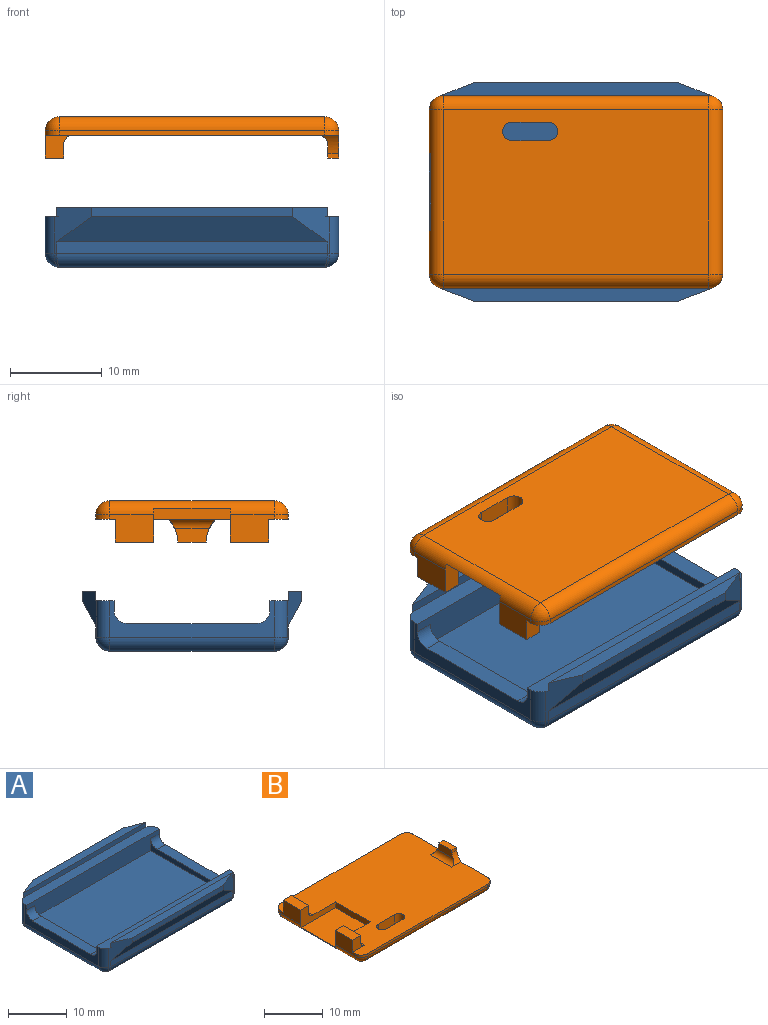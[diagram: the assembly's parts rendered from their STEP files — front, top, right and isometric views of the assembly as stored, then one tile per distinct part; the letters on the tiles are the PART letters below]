
ASSEMBLY  parts=2 mates=1
PART A: 46 faces, bbox 32x24x6.5 mm
  f0: plane 32x2mm, normal (0,0,1), area 63mm2, adj f1,f3,f10,f14,f22,f25,f36,f40
  f1: plane 17.97x4mm, normal (1,0,0), area 30.3mm2, adj f0,f5,f8,f10,f13,f27,f34,f40
  f2: plane 29.5x1.25mm, normal (0,1,0), area 36.9mm2, adj f19,f23,f24,f28
  f3: plane 17.97x4mm, normal (-1,0,0), area 30.3mm2, adj f0,f5,f8,f10,f12,f32,f36,f38
  f4: plane 29.5x1.25mm, normal (0,-1,0), area 36.9mm2, adj f16,f22,f25,f31
  f5: plane 32x2mm, normal (0,0,1), area 63mm2, adj f1,f3,f8,f18,f23,f24,f34,f38
  f6: plane 29x18mm, normal (0,0,-1), area 522mm2, adj f26,f27,f28,f29,f30,f31,f32,f33
  f7: plane 17x2.5mm, normal (-1,0,0), area 18mm2, adj f8,f10,f11,f13,f44,f45
  f8: plane 32x3.5mm, normal (0,-1,0), area 102mm2, adj f1,f3,f5,f7,f9,f11,f43,f44
  f9: plane 17x2.5mm, normal (1,0,0), area 18mm2, adj f8,f10,f11,f12,f42,f43
  f10: plane 32x3.5mm, normal (0,1,0), area 102mm2, adj f0,f1,f3,f7,f9,f11,f42,f45
  f11: plane 28x17mm, normal (0,0,1), area 476mm2, adj f7,f8,f9,f10
  f12: plane 14x2mm, normal (0,0,1), area 28mm2, adj f3,f9,f42,f43
  f13: plane 14x2mm, normal (0,0,1), area 28mm2, adj f1,f7,f44,f45
  f14: plane 29.5x1mm, normal (0,1,0), area 29.5mm2, adj f0,f17,f22,f25
  f15: plane 22x1mm, normal (0,-1,0), area 22mm2, adj f16,f17,f22,f25
  f16: plane 29.5x2.75mm, normal (0,-0.88,-0.48), area 80.7mm2, adj f4,f15,f22,f25
  f17: plane 29.5x1.5mm, normal (0,0,1), area 38.6mm2, adj f14,f15,f22,f25
  f18: plane 29.5x1mm, normal (0,-1,0), area 29.5mm2, adj f5,f21,f23,f24
  f19: plane 29.5x2.75mm, normal (0,0.88,-0.48), area 80.7mm2, adj f2,f20,f23,f24
  f20: plane 22x1mm, normal (0,1,0), area 22mm2, adj f19,f21,f23,f24
  f21: plane 29.5x1.5mm, normal (0,0,1), area 38.6mm2, adj f18,f20,f23,f24
  f22: plane 5x4.06mm, normal (0.37,-0.93,0), area 10.9mm2, adj f0,f4,f14,f15,f16,f17,f29,f40
  f23: plane 5x4.06mm, normal (-0.37,0.93,0), area 10.9mm2, adj f2,f5,f18,f19,f20,f21,f30,f38
  f24: plane 5x4.06mm, normal (0.37,0.93,0), area 10.9mm2, adj f2,f5,f18,f19,f20,f21,f26,f34
  f25: plane 5x4.06mm, normal (-0.37,-0.93,0), area 10.9mm2, adj f0,f4,f14,f15,f16,f17,f33,f36
  f26: cylinder r=1.5mm len=1.52mm, axis (0.93,-0.37,0), area 0.5mm2, adj f6,f24,f28,f35
  f27: cylinder r=1.5mm len=17.97mm, axis (0,1,0), area 42.3mm2, adj f1,f6,f35,f41
  f28: cylinder r=1.5mm len=29.5mm, axis (-1,0,0), area 69mm2, adj f2,f6,f26,f30
  f29: cylinder r=1.5mm len=1.52mm, axis (-0.93,-0.37,0), area 0.5mm2, adj f6,f22,f31,f41
  f30: cylinder r=1.5mm len=1.52mm, axis (-0.93,-0.37,0), area 0.5mm2, adj f6,f23,f28,f39
  f31: cylinder r=1.5mm len=29.5mm, axis (1,0,0), area 69mm2, adj f4,f6,f29,f33
  f32: cylinder r=1.5mm len=17.97mm, axis (0,-1,0), area 42.3mm2, adj f3,f6,f37,f39
  f33: cylinder r=1.5mm len=1.52mm, axis (0.93,-0.37,0), area 0.5mm2, adj f6,f25,f31,f37
  f34: cylinder r=1.5mm len=4mm, axis (0,0,1), area 7.1mm2, adj f1,f5,f24,f35
  f35: sphere r=1.5mm, area 2.7mm2, adj f26,f27,f34
  f36: cylinder r=1.5mm len=4mm, axis (0,0,1), area 7.1mm2, adj f0,f3,f25,f37
  f37: sphere r=1.5mm, area 2.7mm2, adj f32,f33,f36
  f38: cylinder r=1.5mm len=4mm, axis (0,0,-1), area 7.1mm2, adj f3,f5,f23,f39
  f39: sphere r=1.5mm, area 2.7mm2, adj f30,f32,f38
  f40: cylinder r=1.5mm len=4mm, axis (0,0,-1), area 7.1mm2, adj f0,f1,f22,f41
  f41: sphere r=1.5mm, area 2.7mm2, adj f27,f29,f40
  f42: cylinder r=1.5mm len=2mm, axis (1,0,0), area 4.7mm2, adj f3,f9,f10,f12
  f43: cylinder r=1.5mm len=2mm, axis (-1,0,0), area 4.7mm2, adj f3,f8,f9,f12
  f44: cylinder r=1.5mm len=2mm, axis (-1,0,0), area 4.7mm2, adj f1,f7,f8,f13
  f45: cylinder r=1.5mm len=2mm, axis (1,0,0), area 4.7mm2, adj f1,f7,f10,f13
PART B: 42 faces, bbox 32x21x4.5 mm
  f0: plane 4.8x3mm, normal (-1,0,0), area 12.9mm2, adj f1,f2,f9,f22,f24,f30
  f1: plane 32x21mm, normal (0,0,1), area 551mm2, adj f0,f3,f5,f6,f7,f9,f11,f13
  f2: cylinder r=1.5mm len=18mm, axis (0,-1,0), area 36.3mm2, adj f0,f7,f8,f10,f15,f22,f26,f29
  f3: plane 18x3mm, normal (1,0,0), area 18.4mm2, adj f1,f11,f16,f19,f20,f21,f32,f33
  f4: plane 3.79x1.5mm, normal (-1,0,0), area 5mm2, adj f20,f21,f32,f33,f34,f37
  f5: plane 29x0.5mm, normal (0,-1,0), area 14.5mm2, adj f1,f13,f17,f19
  f6: plane 29x0.5mm, normal (0,1,0), area 14.5mm2, adj f1,f9,f11,f12
  f7: plane 4.8x3mm, normal (-1,0,0), area 12.9mm2, adj f1,f2,f13,f26,f27,f31
  f8: plane 29x18mm, normal (0,0,-1), area 510.9mm2, adj f2,f12,f16,f17,f38,f39,f40,f41
  f9: cylinder r=1.5mm len=1.5mm, axis (0,0,1), area 1.2mm2, adj f0,f1,f6,f10
  f10: sphere r=1.5mm, area 3.5mm2, adj f2,f9,f12
  f11: cylinder r=1.5mm len=1.5mm, axis (0,0,-1), area 1.2mm2, adj f1,f3,f6,f14
  f12: cylinder r=1.5mm len=29mm, axis (-1,0,0), area 68.3mm2, adj f6,f8,f10,f14
  f13: cylinder r=1.5mm len=1.5mm, axis (0,0,-1), area 1.2mm2, adj f1,f5,f7,f15
  f14: sphere r=1.5mm, area 3.5mm2, adj f11,f12,f16
  f15: sphere r=1.5mm, area 3.5mm2, adj f2,f13,f17
  f16: cylinder r=1.5mm len=18mm, axis (0,1,0), area 42.4mm2, adj f3,f8,f14,f18
  f17: cylinder r=1.5mm len=29mm, axis (1,0,0), area 68.3mm2, adj f5,f8,f15,f18
  f18: sphere r=1.5mm, area 3.5mm2, adj f16,f17,f19
  f19: cylinder r=1.5mm len=1.5mm, axis (0,0,1), area 1.2mm2, adj f1,f3,f5,f18
  f20: cylinder r=3.99mm len=2.2mm, axis (1,0,0), area 3mm2, adj f1,f3,f4,f33,f37
  f21: cylinder r=3.99mm len=2.2mm, axis (1,0,0), area 3mm2, adj f1,f3,f4,f32,f37
  f22: plane 8.5x3.7mm, normal (0,-1,0), area 15.4mm2, adj f0,f1,f2,f23,f28,f29,f30,f36
  f23: plane 4.2x1.5mm, normal (1,0,0), area 6.3mm2, adj f22,f24,f30,f36
  f24: plane 3x2.5mm, normal (0,1,0), area 5.2mm2, adj f0,f1,f23,f30,f36
  f25: plane 4.2x1.5mm, normal (1,0,0), area 6.3mm2, adj f26,f27,f31,f35
  f26: plane 8.5x3.7mm, normal (0,1,0), area 15.4mm2, adj f1,f2,f7,f25,f28,f29,f31,f35
  f27: plane 3x2.5mm, normal (0,-1,0), area 5.2mm2, adj f1,f7,f25,f31,f35
  f28: plane 8.4x1.2mm, normal (-1,0,0), area 10.1mm2, adj f1,f22,f26,f29
  f29: plane 8.4x8.33mm, normal (0,0,1), area 69.9mm2, adj f2,f22,f26,f28
  f30: plane 4.2x2mm, normal (0,0,1), area 8.4mm2, adj f0,f22,f23,f24
  f31: plane 4.2x2mm, normal (0,0,1), area 8.4mm2, adj f7,f25,f26,f27
  f32: plane 1.2x0.5mm, normal (0,-1,0), area 0.6mm2, adj f3,f4,f21,f34
  f33: plane 1.2x0.5mm, normal (0,1,0), area 0.6mm2, adj f3,f4,f20,f34
  f34: plane 3.14x1.2mm, normal (0,0,1), area 3.8mm2, adj f3,f4,f32,f33
  f35: cylinder r=1mm len=4.2mm, axis (0,1,0), area 6.6mm2, adj f1,f25,f26,f27
  f36: cylinder r=1mm len=4.2mm, axis (0,1,0), area 6.6mm2, adj f1,f22,f23,f24
  f37: cylinder r=1mm len=5.16mm, axis (0,-1,0), area 7.2mm2, adj f1,f4,f20,f21
  f38: cylinder r=1mm len=2mm, axis (0,0,-1), area 6.3mm2, adj f1,f8,f39,f40
  f39: plane 4x2mm, normal (0,1,0), area 8mm2, adj f1,f8,f38,f41
  f40: plane 4x2mm, normal (0,-1,0), area 8mm2, adj f1,f8,f38,f41
  f41: cylinder r=1mm len=2mm, axis (0,0,-1), area 6.3mm2, adj f1,f8,f39,f40
PLACE A t=(-3.67,0.48,-2.69)mm fixed
PLACE B rot(axis=(1,0,0),180deg) t=(-0.07,-0.12,13.7)mm
MATE parallel B.f1 <-> A.f0  axis (0,0,-1) through (-0.07,-10.62,11.7)mm
